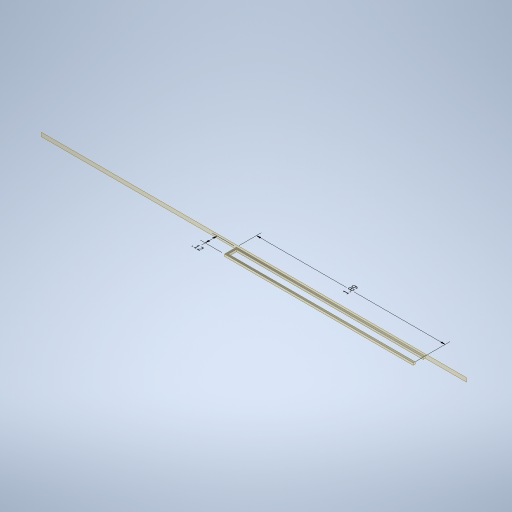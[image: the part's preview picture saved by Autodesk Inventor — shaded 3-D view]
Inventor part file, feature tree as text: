
AUTODESK INVENTOR PART (.ipt)
format: ipt  version: 2024.2 (Build 282272000, 272)  size: 275,456 bytes
history: native  units: in
note: dims shown in document units (in); Inventor stores cm internally (conversion verified against a paired STEP export)
features: other x3, plane x3, sketch x2, sweep x1
ambient origin geometry x8: Origin, YZ Plane, XZ Plane, XY Plane, X Axis, Y Axis, Z Axis, Center Point
bodies: Solid1 (feature_tree)
feature tree (9):
  other  "Annotations"
  sweep  "Sweep1"
  plane  "Work Plane1"
  plane  "Work Plane2"
  plane  "Work Plane4"
  sketch  "Sketch1"  dims[d6=0.0in d7=0.0in d11=0.25in d19=-0.25in]
  sketch  "Sketch2"  dims[d69=1.875in d70=1.875in d86=-0.1175in d89=0.1in d90=0.0in d91=0.0in d92=0.0in d98=0.02in d99=0.02in d100=0.1997in d101=1.885in d102=0.2692in d103=0.1197in d104=0.12in]
  other  "Linear Dimension 1"
  other  "Linear Dimension 2"
